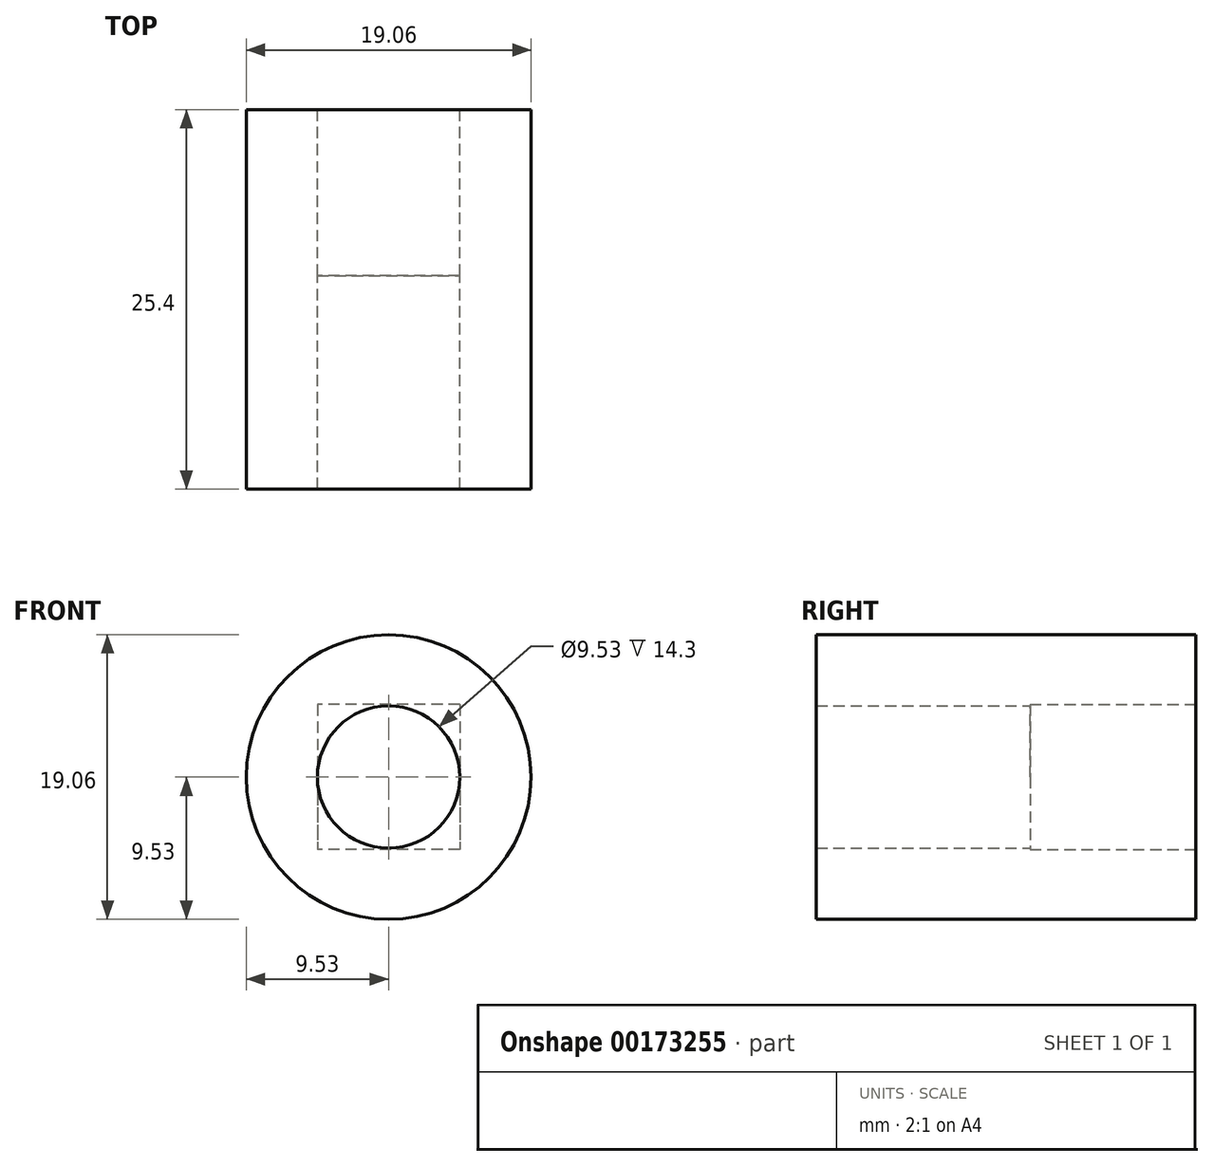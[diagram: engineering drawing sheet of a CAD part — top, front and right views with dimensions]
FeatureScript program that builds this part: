
annotation { "Feature Type Name" : "Feature", "Feature Type Description" : "" }
export const myFeature = defineFeature(function(context is Context, id is Id, definition is map)
    precondition{}
    {
        {
            var Q0;
            Q0=qCreatedBy(makeId("Front.planeOp"),FACE);
            var sketch = newSketch(context, id + "F0", { "sketchPlane" : qUnion([Q0])});
            skCircle(sketch, "E0", {"center": v(0, 0) * mm, "radius": 9.53 * mm});
            skSolve(sketch);
        }
        {
            var Q0;
            Q0 = qSketchRegion(id + "F0", true);
            extrude(context, id + "F1", {"entities" : qUnion([Q0]), "depth" : 25.4 * mm});
        }
        {
            var Q0;
            Q0=qCreatedBy(makeId("Front.planeOp"),FACE);
            var sketch = newSketch(context, id + "F2", { "sketchPlane" : qUnion([Q0])});
            skLineSegment(sketch, "E1.bottom", {"start": v(-4.76, 4.76) * mm, "end": v(4.76, 4.76) * mm});
            skLineSegment(sketch, "E1.top", {"start": v(-4.76, -4.76) * mm, "end": v(4.76, -4.76) * mm});
            skLineSegment(sketch, "E1.left", {"start": v(-4.76, 4.76) * mm, "end": v(-4.76, -4.76) * mm});
            skLineSegment(sketch, "E1.right", {"start": v(4.76, 4.76) * mm, "end": v(4.76, -4.76) * mm});
            skPoint(sketch, "E1.middle", {"position": v(0, 0) * mm});
            skCircle(sketch, "E2", {"center": v(0, 0) * mm, "radius": 4.76 * mm});
            skSolve(sketch);
        }
        {
            var Q0;
            {var subQ0=sQuery(id+"F2.wireOp",EDGE,"E2");var subQ1=makeQuery(id+"F2.imprint","INTERSECT",VERTEX,{"derivedFrom":[sQuery(id+"F2.wireOp",EDGE,"E1.bottom"),subQ0]});Q0=makeQuery(id+"F2.imprint","IMPRINT",FACE,{"disambiguationData":[TD([[makeQuery(id+"F2.imprint","IMPRINT",EDGE,{"disambiguationData":[TD([[subQ1,1.0]])],"derivedFrom":subQ0}),1.0]])]});}
            extrude(context, id + "F3", {"entities" : qUnion([Q0]), "operationType" : NewBodyOperationType.REMOVE, "endBound" : BoundingType.THROUGH_ALL, "depth" : 25.4 * mm});
        }
        {
            var Q0;
            Q0=qCreatedBy(makeId("Front.planeOp"),FACE);
            var sketch = newSketch(context, id + "F4", { "sketchPlane" : qUnion([Q0])});
            skLineSegment(sketch, "E3.bottom", {"start": v(4.76, 4.86) * mm, "end": v(-4.76, 4.86) * mm});
            skLineSegment(sketch, "E3.top", {"start": v(4.76, -4.86) * mm, "end": v(-4.76, -4.86) * mm});
            skLineSegment(sketch, "E3.left", {"start": v(4.76, 4.86) * mm, "end": v(4.76, -4.86) * mm});
            skLineSegment(sketch, "E3.right", {"start": v(-4.76, 4.86) * mm, "end": v(-4.76, -4.86) * mm});
            skPoint(sketch, "E3.middle", {"position": v(0, 0) * mm});
            skSolve(sketch);
        }
        {
            var Q0;
            Q0 = qSketchRegion(id + "F4", true);
            extrude(context, id + "F5", {"entities" : qUnion([Q0]), "operationType" : NewBodyOperationType.REMOVE, "depth" : 11.1 * mm});
        }
    });
